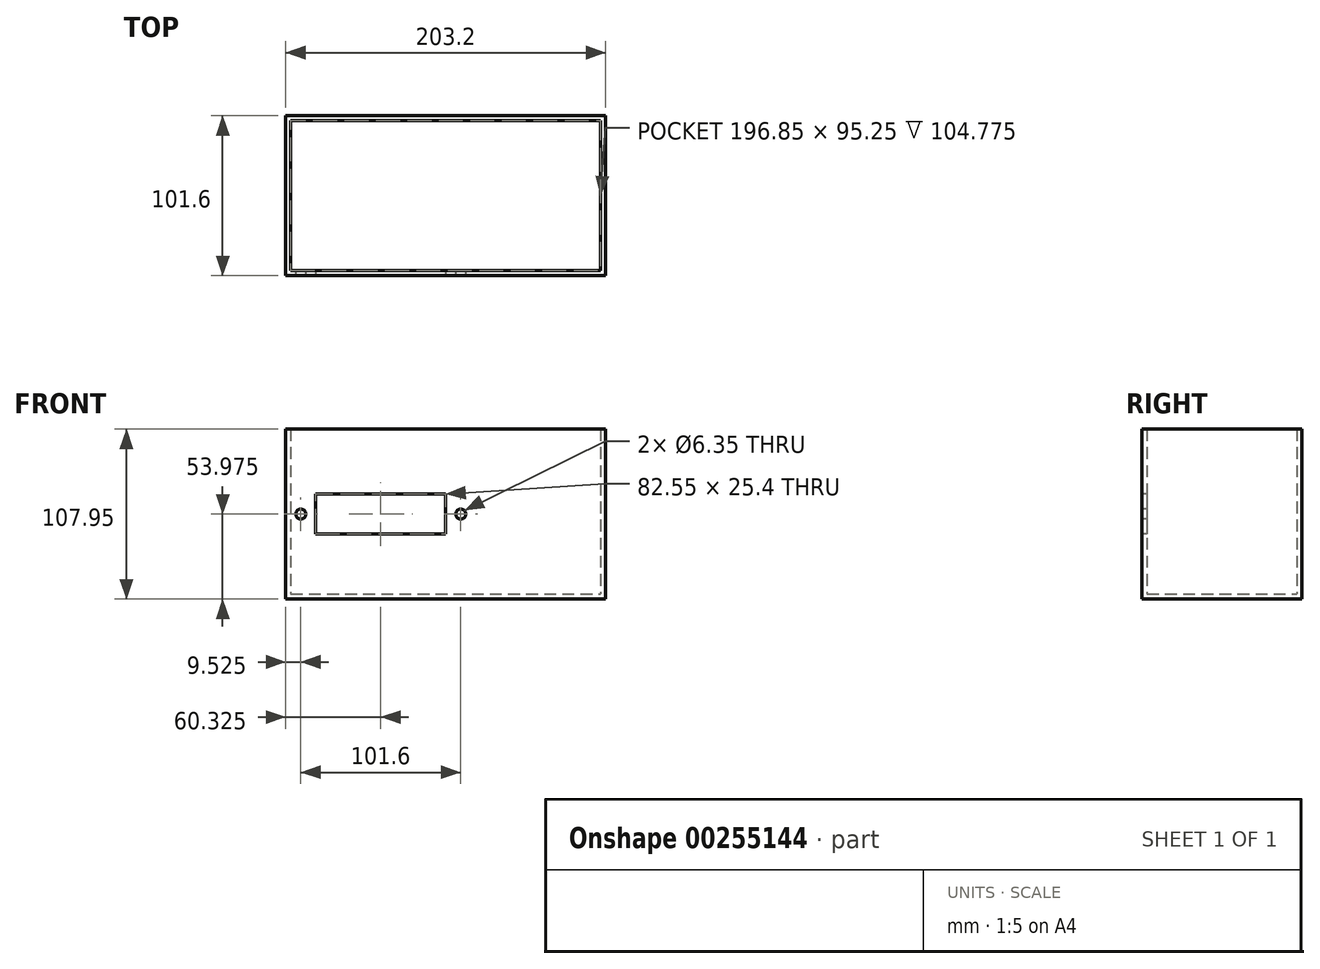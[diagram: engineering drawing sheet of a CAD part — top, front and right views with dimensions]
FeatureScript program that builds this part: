
annotation { "Feature Type Name" : "Feature", "Feature Type Description" : "" }
export const myFeature = defineFeature(function(context is Context, id is Id, definition is map)
    precondition{}
    {
        {
            var Q0;
            Q0=qCreatedBy(makeId("Top.planeOp"),FACE);
            var sketch = newSketch(context, id + "F0", { "sketchPlane" : qUnion([Q0])});
            skLineSegment(sketch, "E0.bottom", {"start": v(-48.95, 0) * mm, "end": v(154.25, 0) * mm});
            skLineSegment(sketch, "E0.top", {"start": v(-48.95, 101.6) * mm, "end": v(154.25, 101.6) * mm});
            skLineSegment(sketch, "E0.left", {"start": v(-48.95, 0) * mm, "end": v(-48.95, 101.6) * mm});
            skLineSegment(sketch, "E0.right", {"start": v(154.25, 0) * mm, "end": v(154.25, 101.6) * mm});
            skSolve(sketch);
        }
        {
            var Q0;
            Q0 = qSketchRegion(id + "F0", true);
            extrude(context, id + "F1", {"entities" : qUnion([Q0]), "depth" : 107.95 * mm});
        }
        {
            var Q0;
            Q0=makeQuery(id+"F1.opExtrude","CAP_FACE",FACE,{"disambiguationData":[OSD([sQuery(id+"F0.wireOp",EDGE,"E0.bottom"),sQuery(id+"F0.wireOp",EDGE,"E0.top"),sQuery(id+"F0.wireOp",EDGE,"E0.left"),sQuery(id+"F0.wireOp",EDGE,"E0.right")])],"isStart":false});
            shell(context, id + "F2", {"entities" : qUnion([Q0]), "thickness" : 3.17 * mm});
        }
        {
            var Q0;
            Q0=qCreatedBy(makeId("Front.planeOp"),FACE);
            var sketch = newSketch(context, id + "F3", { "sketchPlane" : qUnion([Q0])});
            skLineSegment(sketch, "E1.bottom", {"start": v(-29.9, 41.28) * mm, "end": v(52.65, 41.28) * mm});
            skLineSegment(sketch, "E1.top", {"start": v(-29.9, 66.68) * mm, "end": v(52.65, 66.68) * mm});
            skLineSegment(sketch, "E1.left", {"start": v(-29.9, 41.28) * mm, "end": v(-29.9, 66.68) * mm});
            skLineSegment(sketch, "E1.right", {"start": v(52.65, 41.28) * mm, "end": v(52.65, 66.68) * mm});
            skSolve(sketch);
        }
        {
            var Q0;
            Q0 = qSketchRegion(id + "F3", true);
            extrude(context, id + "F4", {"entities" : qUnion([Q0]), "operationType" : NewBodyOperationType.REMOVE, "oppositeDirection" : true, "depth" : 25.4 * mm});
        }
        {
            var Q0;
            Q0=qCreatedBy(makeId("Front.planeOp"),FACE);
            var sketch = newSketch(context, id + "F5", { "sketchPlane" : qUnion([Q0])});
            skLineSegment(sketch, "E2.bottom", {"start": v(-45.77, 34.93) * mm, "end": v(68.53, 34.93) * mm});
            skLineSegment(sketch, "E2.top", {"start": v(-45.77, 73.03) * mm, "end": v(68.53, 73.03) * mm});
            skLineSegment(sketch, "E2.left", {"start": v(-45.77, 34.93) * mm, "end": v(-45.77, 73.03) * mm});
            skLineSegment(sketch, "E2.right", {"start": v(68.53, 34.93) * mm, "end": v(68.53, 73.03) * mm});
            skSolve(sketch);
        }
        {
            var Q0;
            Q0=qCreatedBy(makeId("Front.planeOp"),FACE);
            var sketch = newSketch(context, id + "F6", { "sketchPlane" : qUnion([Q0])});
            skCircle(sketch, "E3", {"center": v(-39.42, 53.98) * mm, "radius": 3.18 * mm});
            skSolve(sketch);
        }
        {
            var Q0;
            Q0 = qSketchRegion(id + "F6", true);
            extrude(context, id + "F7", {"entities" : qUnion([Q0]), "operationType" : NewBodyOperationType.REMOVE, "oppositeDirection" : true, "depth" : 25.4 * mm});
        }
        {
            var Q0;
            Q0=qCreatedBy(makeId("Front.planeOp"),FACE);
            var sketch = newSketch(context, id + "F8", { "sketchPlane" : qUnion([Q0])});
            skCircle(sketch, "E4", {"center": v(62.18, 53.98) * mm, "radius": 3.18 * mm});
            skSolve(sketch);
        }
        {
            var Q0;
            Q0 = qSketchRegion(id + "F8", true);
            extrude(context, id + "F9", {"entities" : qUnion([Q0]), "operationType" : NewBodyOperationType.REMOVE, "oppositeDirection" : true, "depth" : 25.4 * mm});
        }
    });
